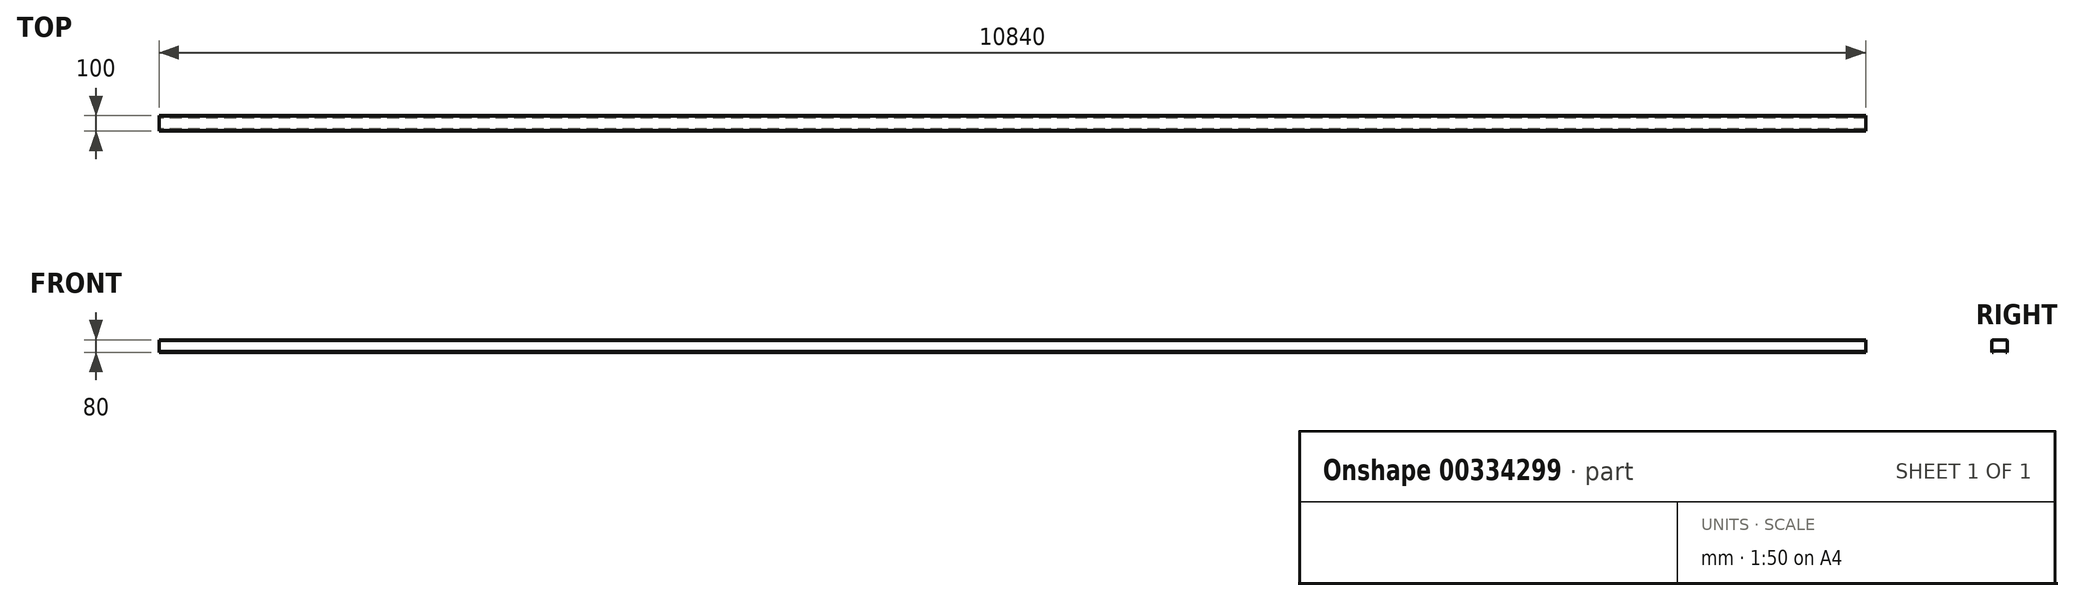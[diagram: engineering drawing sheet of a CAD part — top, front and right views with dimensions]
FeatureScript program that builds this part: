
annotation { "Feature Type Name" : "Feature", "Feature Type Description" : "" }
export const myFeature = defineFeature(function(context is Context, id is Id, definition is map)
    precondition{}
    {
        {
            var Q0;
            Q0=qCreatedBy(makeId("Right.planeOp"),FACE);
            var sketch = newSketch(context, id + "F0", { "sketchPlane" : qUnion([Q0])});
            skLineSegment(sketch, "E0.left", {"start": v(0, 0) * mm, "end": v(0, 80) * mm});
            skLineSegment(sketch, "E1", {"start": v(-50, 80) * mm, "end": v(-50, 0) * mm, "construction": true});
            skLineSegment(sketch, "E2", {"start": v(0, 0) * mm, "end": v(-15, 0) * mm});
            skLineSegment(sketch, "E3", {"start": v(-15, 0) * mm, "end": v(-15, 8) * mm});
            skLineSegment(sketch, "E4", {"start": v(-15, 8) * mm, "end": v(-85, 8) * mm});
            skLineSegment(sketch, "E5", {"start": v(-85, 8) * mm, "end": v(-85, 0) * mm});
            skLineSegment(sketch, "E6", {"start": v(-85, 0) * mm, "end": v(-100, 0) * mm});
            skPoint(sketch, "E7", {"position": v(-100, 80) * mm});
            skLineSegment(sketch, "E8", {"start": v(-100, 80) * mm, "end": v(-100, 0) * mm});
            skLineSegment(sketch, "E9", {"start": v(-100, 80) * mm, "end": v(-100, 80) * mm});
            skLineSegment(sketch, "E10", {"start": v(0, 80) * mm, "end": v(-100, 80) * mm});
            skSolve(sketch);
        }
        {
            var Q0;
            Q0=makeQuery(id+"F0.imprint","IMPRINT",FACE,{"disambiguationData":[TD([[makeQuery(id+"F0.imprint","IMPRINT",EDGE,{"derivedFrom":sQuery(id+"F0.wireOp",EDGE,"E0.top")}),1.0]])]});
            var Q1;
            Q1=makeQuery(id+"F0.imprint","IMPRINT",FACE,{"disambiguationData":[TD([[makeQuery(id+"F0.imprint","IMPRINT",EDGE,{"derivedFrom":sQuery(id+"F0.wireOp",EDGE,"E0.left")}),1.0]])]});
            extrude(context, id + "F1", {"entities" : qUnion([Q0, Q1]), "depth" : 10840 * mm});
        }
        {
            var Q0;
            Q0=makeQuery(id+"F1.opExtrude","SWEPT_EDGE",EDGE,{"disambiguationData":[OSD([sQuery(id+"F0.wireOp",EDGE,"E6"),sQuery(id+"F0.wireOp",EDGE,"E8")])]});
            var Q1;
            Q1=makeQuery(id+"F1.opExtrude","SWEPT_EDGE",EDGE,{"disambiguationData":[OSD([sQuery(id+"F0.wireOp",EDGE,"E8"),sQuery(id+"F0.wireOp",EDGE,"E10")])]});
            var Q2;
            Q2=makeQuery(id+"F1.opExtrude","SWEPT_EDGE",EDGE,{"disambiguationData":[OSD([sQuery(id+"F0.wireOp",EDGE,"E0.left"),sQuery(id+"F0.wireOp",EDGE,"E10")])]});
            var Q3;
            Q3=makeQuery(id+"F1.opExtrude","SWEPT_EDGE",EDGE,{"disambiguationData":[OSD([sQuery(id+"F0.wireOp",EDGE,"E0.left"),sQuery(id+"F0.wireOp",EDGE,"E2")])]});
            var Q4;
            Q4=makeQuery(id+"F1.opExtrude","SWEPT_EDGE",EDGE,{"disambiguationData":[OSD([sQuery(id+"F0.wireOp",EDGE,"E2"),sQuery(id+"F0.wireOp",EDGE,"E3")])]});
            var Q5;
            Q5=makeQuery(id+"F1.opExtrude","SWEPT_EDGE",EDGE,{"disambiguationData":[OSD([sQuery(id+"F0.wireOp",EDGE,"E5"),sQuery(id+"F0.wireOp",EDGE,"E6")])]});
            chamfer(context, id + "F2", {"entities" : qUnion([Q0, Q1, Q2, Q3, Q4, Q5]), "width" : 5 * mm, "tangentPropagation" : true});
        }
    });
